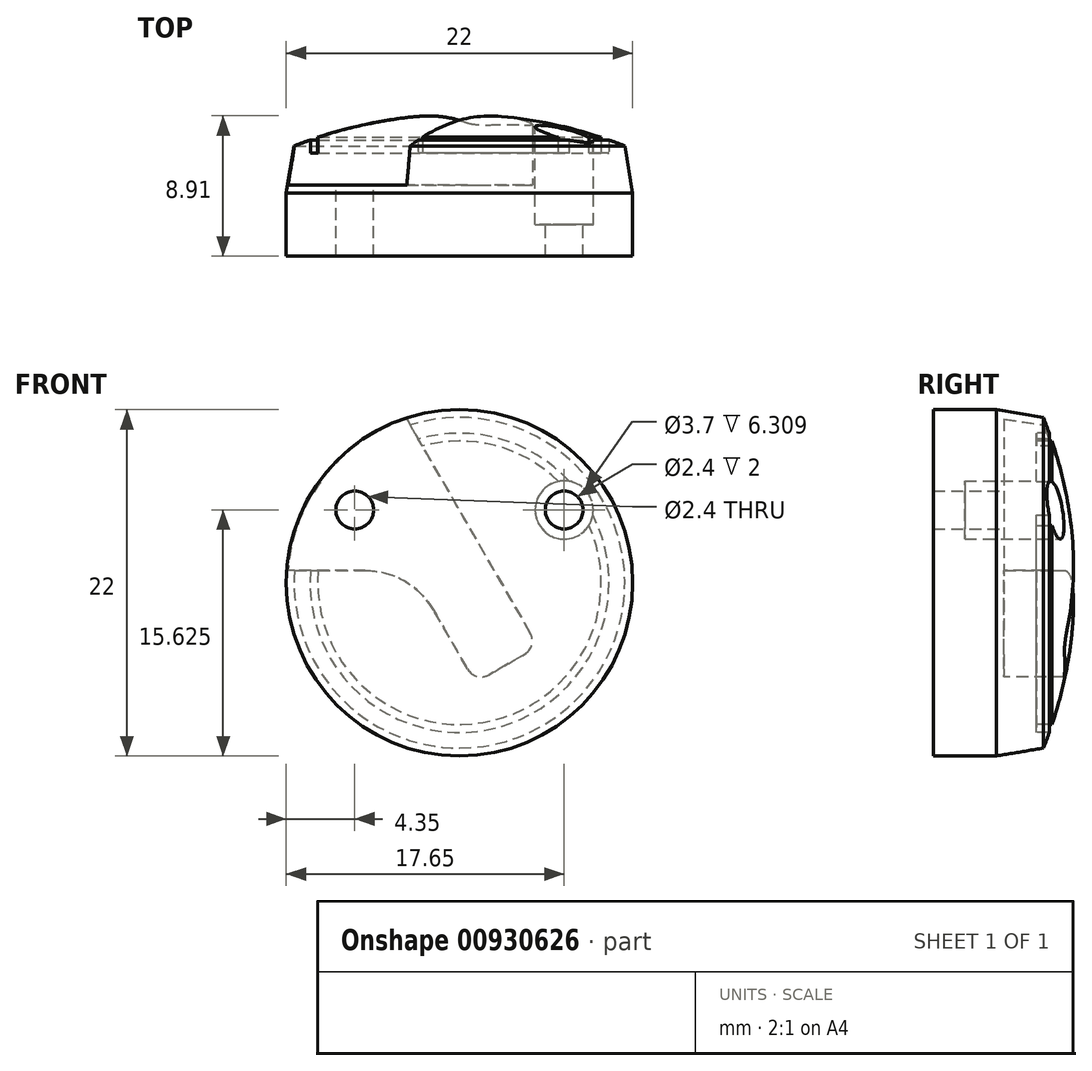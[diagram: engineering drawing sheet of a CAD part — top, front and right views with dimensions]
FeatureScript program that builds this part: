
annotation { "Feature Type Name" : "Feature", "Feature Type Description" : "" }
export const myFeature = defineFeature(function(context is Context, id is Id, definition is map)
    precondition{}
    {
        {
            var Q0;
            Q0=qCreatedBy(makeId("Top.planeOp"),FACE);
            var sketch = newSketch(context, id + "F0", { "sketchPlane" : qUnion([Q0])});
            skLineSegment(sketch, "E0", {"start": v(0, 0) * mm, "end": v(0, 9) * mm});
            skLineSegment(sketch, "E1", {"start": v(0, 0) * mm, "end": v(11, 0) * mm});
            skLineSegment(sketch, "E2", {"start": v(11, 0) * mm, "end": v(11, 4) * mm});
            skLineSegment(sketch, "E3", {"start": v(11, 4) * mm, "end": v(10.5, 7) * mm});
            skArc(sketch, "E4", {"start": v(10.5, 7) * mm, "mid": v(10, 7.2) * mm, "end": v(9.5, 7.37) * mm});
            skLineSegment(sketch, "E5", {"start": v(0, 9) * mm, "end": v(11, 9) * mm, "construction": true});
            skLineSegment(sketch, "E6", {"start": v(11, 9) * mm, "end": v(11, 0) * mm, "construction": true});
            skLineSegment(sketch, "E7", {"start": v(9, 7.54) * mm, "end": v(9, 6.54) * mm});
            skLineSegment(sketch, "E8", {"start": v(9, 6.54) * mm, "end": v(9.5, 6.54) * mm});
            skLineSegment(sketch, "E9", {"start": v(9.5, 6.54) * mm, "end": v(9.5, 7.37) * mm});
            skArc(sketch, "E10.trimOffspring", {"start": v(9, 7.54) * mm, "mid": v(4.56, 8.63) * mm, "end": v(0, 9) * mm});
            skSolve(sketch);
        }
        {
            var Q0;
            Q0=qSketchRegion(id+"F0",true);
            var Q1;
            Q1=sQuery(id+"F0.wireOp",EDGE,"E0");
            revolve(context, id + "F1", {"entities" : qUnion([Q0]), "axis" : qUnion([Q1]), "revolveType" : RevolveType.FULL});
        }
        {
            var Q0;
            Q0=qCreatedBy(makeId("Front.planeOp"),FACE);
            cPlane(context, id + "F2", {"entities" : qUnion([Q0]), "cplaneType" : CPlaneType.OFFSET, "offset" : 9 * mm, "oppositeDirection" : true, "width" : 150 * mm, "height" : 150 * mm});
        }
        {
            var Q0;
            Q0=qCreatedBy(id+"F2.planeOp",FACE);
            var sketch = newSketch(context, id + "F3", { "sketchPlane" : qUnion([Q0])});
            skCircle(sketch, "E11", {"center": v(6.65, 4.62) * mm, "radius": 1.85 * mm});
            skSolve(sketch);
        }
        {
            var Q0;
            Q0=qSketchRegion(id+"F3",true);
            extrude(context, id + "F4", {"entities" : qUnion([Q0]), "operationType" : NewBodyOperationType.REMOVE, "depth" : 7 * mm, "offsetDistance" : 25 * mm});
        }
        {
            var Q0;
            Q0=makeQuery(id+"F4.boolean.opBoolean","COPY",FACE,{"derivedFrom":makeQuery(id+"F4.opExtrude","CAP_FACE",FACE,{"disambiguationData":[OSD([sQuery(id+"F3.wireOp",EDGE,"E11")])],"isStart":false})});
            var sketch = newSketch(context, id + "F5", { "sketchPlane" : qUnion([Q0])});
            skCircle(sketch, "E12", {"center": v(-6.65, 4.62) * mm, "radius": 1.2 * mm});
            skSolve(sketch);
        }
        {
            var Q0;
            Q0=qSketchRegion(id+"F5",true);
            extrude(context, id + "F6", {"entities" : qUnion([Q0]), "operationType" : NewBodyOperationType.REMOVE, "endBound" : BoundingType.UP_TO_NEXT, "oppositeDirection" : true, "depth" : 25 * mm, "offsetDistance" : 25 * mm});
        }
        {
            var Q0;
            Q0=qCreatedBy(id+"F2.planeOp",FACE);
            var sketch = newSketch(context, id + "F7", { "sketchPlane" : qUnion([Q0])});
            skLineSegment(sketch, "E13", {"start": v(5.5, -9.53) * mm, "end": v(-5.5, 9.53) * mm, "construction": true});
            skLineSegment(sketch, "E14", {"start": v(-3.39, 10.47) * mm, "end": v(5, -4.05) * mm});
            skLineSegment(sketch, "E15", {"start": v(1, -6.35) * mm, "end": v(-3.1, 0.78) * mm});
            skArc(sketch, "E16", {"start": v(-3.39, 10.47) * mm, "mid": v(-8.66, 6.78) * mm, "end": v(-10.97, 0.77) * mm});
            skLineSegment(sketch, "E17", {"start": v(5, -4.05) * mm, "end": v(1, -6.35) * mm});
            skLineSegment(sketch, "E18", {"start": v(-3.1, 0.78) * mm, "end": v(-10.97, 0.77) * mm});
            skSolve(sketch);
        }
        {
            var Q0;
            Q0=qSketchRegion(id+"F7",true);
            extrude(context, id + "F8", {"entities" : qUnion([Q0]), "operationType" : NewBodyOperationType.REMOVE, "depth" : 4.5 * mm, "offsetDistance" : 25 * mm});
        }
        {
            var Q0;
            Q0=makeQuery(id+"F8.boolean.opBoolean","COPY",EDGE,{"derivedFrom":makeQuery(id+"F8.opExtrude","SWEPT_EDGE",EDGE,{"disambiguationData":[OSD([sQuery(id+"F7.wireOp",EDGE,"E14"),sQuery(id+"F7.wireOp",EDGE,"E17")])]})});
            var Q1;
            Q1=makeQuery(id+"F8.boolean.opBoolean","COPY",EDGE,{"derivedFrom":makeQuery(id+"F8.opExtrude","SWEPT_EDGE",EDGE,{"disambiguationData":[OSD([sQuery(id+"F7.wireOp",EDGE,"E15"),sQuery(id+"F7.wireOp",EDGE,"E17")])]})});
            fillet(context, id + "F9", {"entities" : qUnion([Q0, Q1]), "radius" : 1 * mm, "tangentPropagation" : true, "allowEdgeOverflow" : false});
        }
        {
            var Q0;
            Q0=makeQuery(id+"F8.boolean.opBoolean","COPY",FACE,{"derivedFrom":makeQuery(id+"F8.opExtrude","CAP_FACE",FACE,{"disambiguationData":[OSD([sQuery(id+"F7.wireOp",EDGE,"E14"),sQuery(id+"F7.wireOp",EDGE,"E15"),sQuery(id+"F7.wireOp",EDGE,"E16"),sQuery(id+"F7.wireOp",EDGE,"E17"),sQuery(id+"F7.wireOp",EDGE,"E18")])],"isStart":false})});
            var sketch = newSketch(context, id + "F10", { "sketchPlane" : qUnion([Q0])});
            skCircle(sketch, "E19", {"center": v(6.65, 4.62) * mm, "radius": 1.2 * mm});
            skSolve(sketch);
        }
        {
            var Q0;
            Q0=qSketchRegion(id+"F10",true);
            extrude(context, id + "F11", {"entities" : qUnion([Q0]), "operationType" : NewBodyOperationType.REMOVE, "endBound" : BoundingType.UP_TO_NEXT, "oppositeDirection" : true, "depth" : 25 * mm, "offsetDistance" : 25 * mm});
        }
        {
            var Q0;
            Q0=makeQuery(id+"F8.boolean.opBoolean","COPY",EDGE,{"derivedFrom":makeQuery(id+"F8.opExtrude","SWEPT_EDGE",EDGE,{"disambiguationData":[OSD([sQuery(id+"F7.wireOp",EDGE,"E15"),sQuery(id+"F7.wireOp",EDGE,"E18")])]})});
            fillet(context, id + "F12", {"entities" : qUnion([Q0]), "radius" : 5 * mm, "tangentPropagation" : true, "allowEdgeOverflow" : false});
        }
    });
